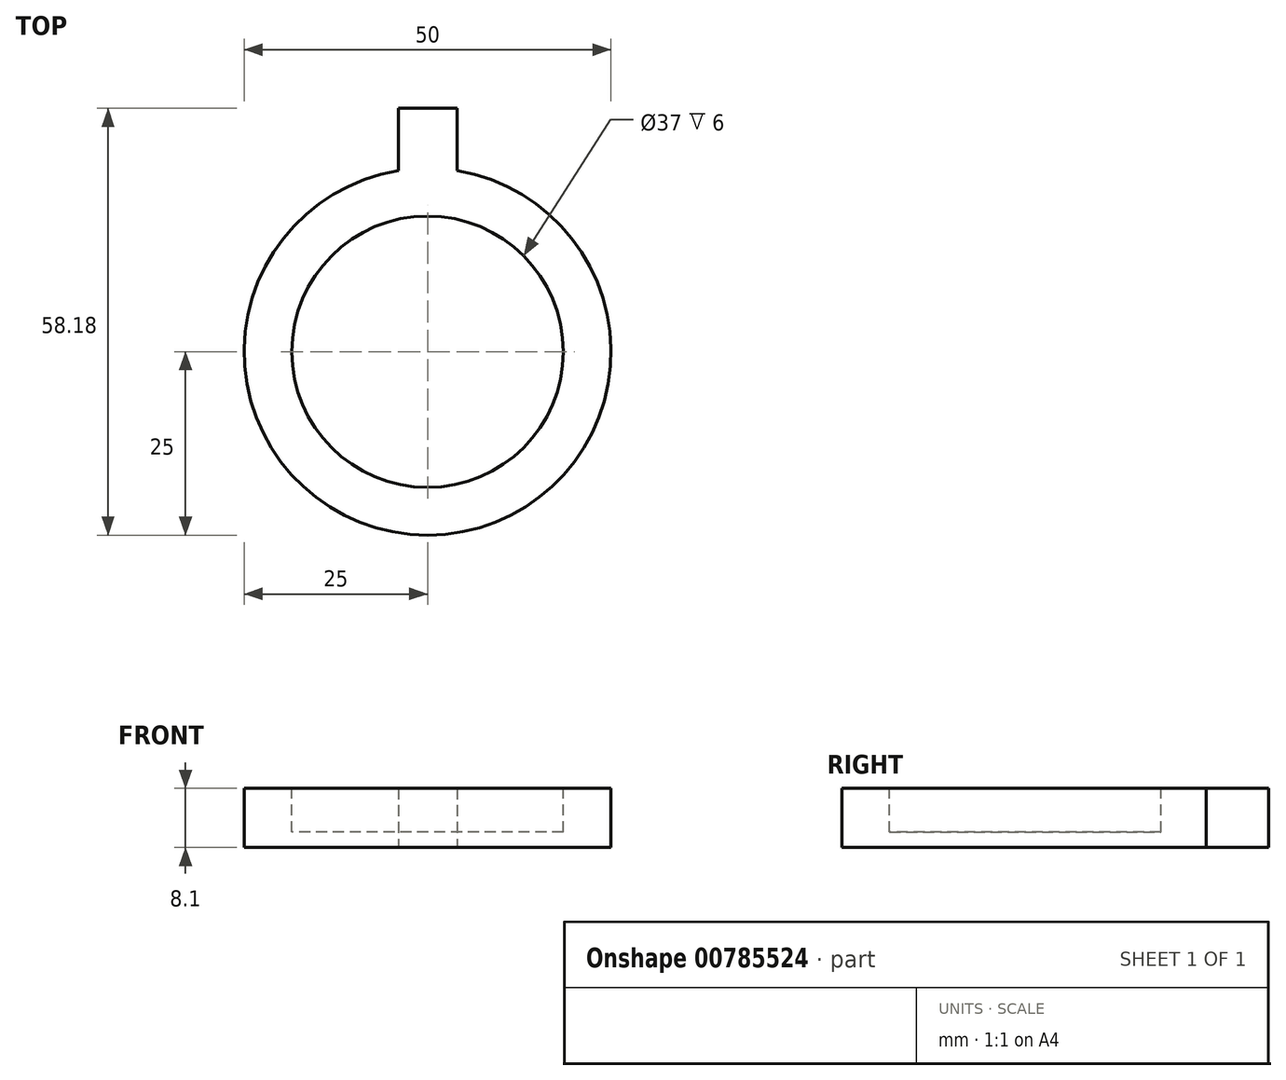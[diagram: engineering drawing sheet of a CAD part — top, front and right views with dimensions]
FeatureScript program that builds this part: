
annotation { "Feature Type Name" : "Feature", "Feature Type Description" : "" }
export const myFeature = defineFeature(function(context is Context, id is Id, definition is map)
    precondition{}
    {
        {
            var Q0;
            Q0=qCreatedBy(makeId("Top.planeOp"),FACE);
            var sketch = newSketch(context, id + "F0", { "sketchPlane" : qUnion([Q0])});
            skCircle(sketch, "E0", {"center": v(0, 0) * mm, "radius": 25 * mm});
            skLineSegment(sketch, "E1", {"start": v(0, -25) * mm, "end": v(0, 25) * mm});
            skLineSegment(sketch, "E2", {"start": v(4, 24.68) * mm, "end": v(4, 33.18) * mm});
            skLineSegment(sketch, "E3", {"start": v(-4, 24.68) * mm, "end": v(-4, 33.18) * mm});
            skLineSegment(sketch, "E4", {"start": v(-4, 33.18) * mm, "end": v(4, 33.18) * mm});
            skSolve(sketch);
        }
        {
            var Q0;
            {var subQ0=sQuery(id+"F0.wireOp",EDGE,"E1");Q0=makeQuery(id+"F0.imprint","IMPRINT",FACE,{"disambiguationData":[TD([[makeQuery(id+"F0.imprint","IMPRINT",EDGE,{"derivedFrom":subQ0}),1.0]])]});}
            var Q1;
            {var subQ0=sQuery(id+"F0.wireOp",EDGE,"E1");Q1=makeQuery(id+"F0.imprint","IMPRINT",FACE,{"disambiguationData":[TD([[makeQuery(id+"F0.imprint","IMPRINT",EDGE,{"derivedFrom":subQ0}),-1.0]])]});}
            var Q2;
            {var subQ3=sQuery(id+"F0.wireOp",EDGE,"E2");Q2=makeQuery(id+"F0.imprint","IMPRINT",FACE,{"disambiguationData":[TD([[makeQuery(id+"F0.imprint","IMPRINT",EDGE,{"derivedFrom":subQ3}),1.0]])]});}
            extrude(context, id + "F1", {"entities" : qUnion([Q0, Q1, Q2]), "depth" : 8.1 * mm, "offsetDistance" : 25 * mm});
        }
        {
            var Q0;
            Q0=makeQuery(id+"F1.opExtrude","SWEPT_FACE",FACE,{"disambiguationData":[OSD([sQuery(id+"F0.wireOp",EDGE,"E4")])]});
            var sketch = newSketch(context, id + "F2", { "sketchPlane" : qUnion([Q0])});
            skLineSegment(sketch, "E5", {"start": v(-4, 3) * mm, "end": v(4, 3) * mm});
            skSolve(sketch);
        }
        {
            var Q0;
            Q0=makeQuery(id+"F1.opExtrude","CAP_FACE",FACE,{"disambiguationData":[OSD([sQuery(id+"F0.wireOp",EDGE,"E0"),sQuery(id+"F0.wireOp",EDGE,"E2"),sQuery(id+"F0.wireOp",EDGE,"E3"),sQuery(id+"F0.wireOp",EDGE,"E4")])],"isStart":false});
            var sketch = newSketch(context, id + "F3", { "sketchPlane" : qUnion([Q0])});
            skCircle(sketch, "E6", {"center": v(0, 0) * mm, "radius": 18.5 * mm});
            skCircle(sketch, "E7", {"center": v(0, 0) * mm, "radius": 19.5 * mm});
            skSolve(sketch);
        }
        {
            var Q0;
            Q0=makeQuery(id+"F3.imprint","IMPRINT",FACE,{"disambiguationData":[TD([[makeQuery(id+"F3.imprint","IMPRINT",EDGE,{"derivedFrom":sQuery(id+"F3.wireOp",EDGE,"E6")}),1.0]])]});
            extrude(context, id + "F4", {"entities" : qUnion([Q0]), "operationType" : NewBodyOperationType.REMOVE, "oppositeDirection" : true, "depth" : 6 * mm, "offsetDistance" : 25 * mm});
        }
    });
